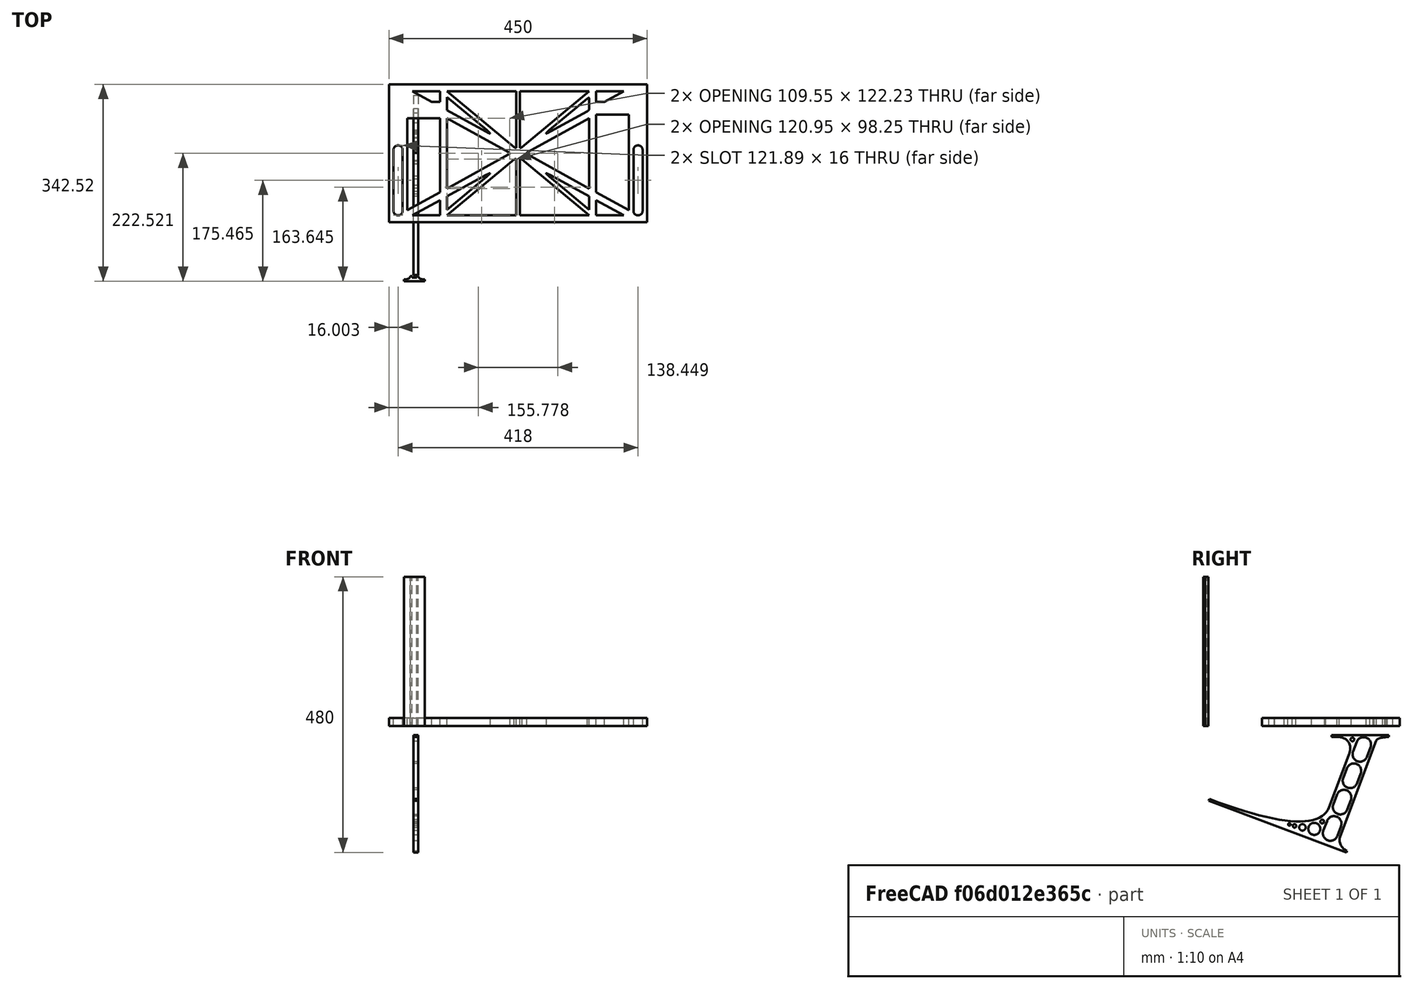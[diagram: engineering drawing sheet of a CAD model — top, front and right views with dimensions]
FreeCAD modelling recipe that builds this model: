
FCSTD DOCUMENT  (FreeCAD 0.19R0.19.2)
Label: laptopStand070
License: All rights reserved
LicenseURL: http://en.wikipedia.org/wiki/All_rights_reserved
objects: Sketcher::SketchObject×3, Part::Extrusion×3
note: 6 computed .brp shape members not serialized (recipe doc carries the construction recipe); baked Part::Feature solids carry a one-line shape summary decoded from their .brp

FEATURE [Sketcher::SketchObject] Sketch
  FullyConstrained = true
  sketch-geometry (140):
    g0: LineSegment StartX=-10.9272 StartY=-82.7794 StartZ=0 EndX=46.0728 EndY=-51.4823 EndZ=0
    g1: LineSegment StartX=366.073 StartY=-91.7794 StartZ=0 EndX=318.073 EndY=-65.424 EndZ=0
    g2: LineSegment StartX=-10.9272 StartY=77.3346 StartZ=0 EndX=-10.9272 EndY=-82.7794 EndZ=0
    g3: LineSegment StartX=375.073 StartY=-82.7794 StartZ=0 EndX=375.073 EndY=83.9235 EndZ=0
    g4: LineSegment StartX=-1.92719 StartY=-91.7794 StartZ=0 EndX=46.0728 EndY=-91.7794 EndZ=0
    g5: LineSegment StartX=318.073 StartY=124.221 StartZ=0 EndX=366.073 EndY=124.221 EndZ=0
    g6: LineSegment StartX=306.073 StartY=124.221 StartZ=0 EndX=189.124 EndY=27.0628 EndZ=0
    g7: LineSegment StartX=58.0728 StartY=-91.7794 StartZ=0 EndX=175.022 EndY=5.37834 EndZ=0
    g8: LineSegment StartX=58.0728 StartY=-81.8102 StartZ=0 EndX=58.0728 EndY=-58.8351 EndZ=0
    g9: LineSegment StartX=306.073 StartY=114.251 StartZ=0 EndX=306.073 EndY=91.2763 EndZ=0
    g10: LineSegment StartX=175.022 StartY=27.0628 StartZ=0 EndX=58.0728 EndY=124.221 EndZ=0
    g11: LineSegment StartX=189.124 StartY=5.37834 StartZ=0 EndX=306.073 EndY=-91.7794 EndZ=0
    g12: LineSegment StartX=306.073 StartY=77.3346 StartZ=0 EndX=306.073 EndY=-44.8935 EndZ=0
    g13: LineSegment StartX=318.073 StartY=83.9235 StartZ=0 EndX=318.073 EndY=-51.4823 EndZ=0
    g14: LineSegment StartX=306.073 StartY=-58.8351 StartZ=0 EndX=306.073 EndY=-81.8102 EndZ=0
    g15: LineSegment StartX=318.073 StartY=-51.4823 StartZ=0 EndX=375.073 EndY=-82.7794 EndZ=0
    g16: LineSegment StartX=318.073 StartY=-65.424 StartZ=0 EndX=318.073 EndY=-91.7794 EndZ=0
    g17: LineSegment StartX=318.073 StartY=-91.7794 StartZ=0 EndX=366.073 EndY=-91.7794 EndZ=0
    g18: LineSegment StartX=58.0728 StartY=-44.8935 StartZ=0 EndX=58.0728 EndY=77.3346 EndZ=0
    g19: LineSegment StartX=46.0728 StartY=-65.424 StartZ=0 EndX=-1.92719 EndY=-91.7794 EndZ=0
    g20: LineSegment StartX=46.0728 StartY=-65.424 StartZ=0 EndX=46.0728 EndY=-91.7794 EndZ=0
    g21: LineSegment StartX=58.0728 StartY=91.2763 StartZ=0 EndX=58.0728 EndY=114.251 EndZ=0
    g22: LineSegment StartX=46.0728 StartY=77.3346 StartZ=0 EndX=46.0728 EndY=-51.4823 EndZ=0
    g23: LineSegment StartX=-42.9272 StartY=136.221 StartZ=0 EndX=-42.9272 EndY=-103.779 EndZ=0
    g24: LineSegment StartX=407.073 StartY=136.221 StartZ=0 EndX=407.073 EndY=-103.779 EndZ=0
    g25: LineSegment StartX=179.022 StartY=27.0628 StartZ=0 EndX=179.022 EndY=124.221 EndZ=0
    g26: LineSegment StartX=185.124 StartY=27.0628 StartZ=0 EndX=185.124 EndY=124.221 EndZ=0
    g27: ArcOfCircle CenterX=-26.9272 CenterY=22.1087 CenterZ=0 NormalX=0 NormalY=0 NormalZ=1 AngleXU=0 Radius=8 StartAngle=1e-16 EndAngle=3.14159
    g28: ArcOfCircle CenterX=-26.9272 CenterY=-83.7794 CenterZ=0 NormalX=0 NormalY=0 NormalZ=1 AngleXU=0 Radius=8 StartAngle=3.14159 EndAngle=6.28319
    g29: LineSegment StartX=-34.9272 StartY=22.1087 StartZ=0 EndX=-34.9272 EndY=-83.7794 EndZ=0
    g30: LineSegment StartX=-18.9272 StartY=22.1087 StartZ=0 EndX=-18.9272 EndY=-83.7794 EndZ=0
    g31: LineSegment StartX=185.124 StartY=-91.7794 StartZ=0 EndX=306.073 EndY=-91.7794 EndZ=0
    g32: LineSegment StartX=179.022 StartY=-91.7794 StartZ=0 EndX=58.0728 EndY=-91.7794 EndZ=0
    g33: LineSegment StartX=306.073 StartY=124.221 StartZ=0 EndX=185.124 EndY=124.221 EndZ=0
    g34: LineSegment StartX=179.022 StartY=124.221 StartZ=0 EndX=58.0728 EndY=124.221 EndZ=0
    g35: ArcOfCircle CenterX=391.073 CenterY=22.1087 CenterZ=0 NormalX=0 NormalY=0 NormalZ=1 AngleXU=0 Radius=8 StartAngle=-4.4e-15 EndAngle=3.14159
    g36: LineSegment StartX=399.073 StartY=22.1087 StartZ=0 EndX=399.073 EndY=-83.7794 EndZ=0
    g37: LineSegment StartX=383.073 StartY=22.1087 StartZ=0 EndX=383.073 EndY=-83.7794 EndZ=0
    g38: ArcOfCircle CenterX=391.073 CenterY=-83.7794 CenterZ=0 NormalX=0 NormalY=0 NormalZ=1 AngleXU=0 Radius=8 StartAngle=3.14159 EndAngle=6.28319
    g39: Circle CenterX=175.022 CenterY=27.0628 CenterZ=0 NormalX=0 NormalY=0 NormalZ=1 AngleXU=0 Radius=1
    g40: Circle CenterX=179.022 CenterY=24.8665 CenterZ=0 NormalX=0 NormalY=0 NormalZ=1 AngleXU=0 Radius=1
    g41: Circle CenterX=179.022 CenterY=27.0628 CenterZ=0 NormalX=0 NormalY=0 NormalZ=1 AngleXU=0 Radius=1
    g42: BSplineCurve PolesCount=3 KnotsCount=2 Degree=2 IsPeriodic=0
    g43: GeomPoint X=175.022 Y=27.0628 Z=0
    g44: GeomPoint X=179.022 Y=27.0628 Z=0
    g45: Circle CenterX=189.124 CenterY=27.0628 CenterZ=0 NormalX=0 NormalY=0 NormalZ=1 AngleXU=0 Radius=1
    g46: Circle CenterX=185.124 CenterY=24.8665 CenterZ=0 NormalX=0 NormalY=0 NormalZ=1 AngleXU=0 Radius=1
    g47: Circle CenterX=185.124 CenterY=27.0628 CenterZ=0 NormalX=0 NormalY=0 NormalZ=1 AngleXU=0 Radius=1
    g48: BSplineCurve PolesCount=3 KnotsCount=2 Degree=2 IsPeriodic=0
    g49: GeomPoint X=189.124 Y=27.0628 Z=0
    g50: GeomPoint X=185.124 Y=27.0628 Z=0
    g51: Circle CenterX=175.022 CenterY=5.37834 CenterZ=0 NormalX=0 NormalY=0 NormalZ=1 AngleXU=0 Radius=1
    g52: Circle CenterX=179.022 CenterY=7.57463 CenterZ=0 NormalX=0 NormalY=0 NormalZ=1 AngleXU=0 Radius=1
    g53: Circle CenterX=179.022 CenterY=5.34704 CenterZ=0 NormalX=0 NormalY=0 NormalZ=1 AngleXU=0 Radius=1
    g54: BSplineCurve PolesCount=3 KnotsCount=2 Degree=2 IsPeriodic=0
    g55: GeomPoint X=175.022 Y=5.37834 Z=0
    g56: GeomPoint X=179.022 Y=5.34704 Z=0
    g57: Circle CenterX=189.124 CenterY=5.37834 CenterZ=0 NormalX=0 NormalY=0 NormalZ=1 AngleXU=0 Radius=1
    g58: Circle CenterX=185.124 CenterY=7.57463 CenterZ=0 NormalX=0 NormalY=0 NormalZ=1 AngleXU=0 Radius=1
    g59: Circle CenterX=185.124 CenterY=5.34704 CenterZ=0 NormalX=0 NormalY=0 NormalZ=1 AngleXU=0 Radius=1
    g60: BSplineCurve PolesCount=3 KnotsCount=2 Degree=2 IsPeriodic=0
    g61: GeomPoint X=189.124 Y=5.37834 Z=0
    g62: GeomPoint X=185.124 Y=5.34704 Z=0
    g63: LineSegment StartX=179.022 StartY=5.34704 StartZ=0 EndX=179.022 EndY=-91.7794 EndZ=0
    g64: LineSegment StartX=185.124 StartY=-91.7794 StartZ=0 EndX=185.124 EndY=5.34704 EndZ=0
    g65: Circle CenterX=165.871 CenterY=18.1458 CenterZ=0 NormalX=0 NormalY=0 NormalZ=1 AngleXU=0 Radius=1
    g66: Circle CenterX=169.377 CenterY=16.2206 CenterZ=0 NormalX=0 NormalY=0 NormalZ=1 AngleXU=0 Radius=1
    g67: Circle CenterX=165.871 CenterY=14.2954 CenterZ=0 NormalX=0 NormalY=0 NormalZ=1 AngleXU=0 Radius=1
    g68: BSplineCurve PolesCount=3 KnotsCount=2 Degree=2 IsPeriodic=0
    g69: GeomPoint X=165.871 Y=18.1458 Z=0
    g70: GeomPoint X=165.871 Y=14.2954 Z=0
    g71: Circle CenterX=198.275 CenterY=18.1458 CenterZ=0 NormalX=0 NormalY=0 NormalZ=1 AngleXU=0 Radius=1
    g72: Circle CenterX=194.768 CenterY=16.2206 CenterZ=0 NormalX=0 NormalY=0 NormalZ=1 AngleXU=0 Radius=1
    g73: Circle CenterX=198.275 CenterY=14.2954 CenterZ=0 NormalX=0 NormalY=0 NormalZ=1 AngleXU=0 Radius=1
    g74: BSplineCurve PolesCount=3 KnotsCount=2 Degree=2 IsPeriodic=0
    g75: GeomPoint X=198.275 Y=18.1458 Z=0
    g76: GeomPoint X=198.275 Y=14.2954 Z=0
    g77: LineSegment StartX=165.871 StartY=18.1458 StartZ=0 EndX=58.0728 EndY=77.3346 EndZ=0
    g78: LineSegment StartX=58.0728 StartY=-44.8935 StartZ=0 EndX=165.871 EndY=14.2954 EndZ=0
    g79: LineSegment StartX=198.275 StartY=18.1458 StartZ=0 EndX=306.073 EndY=77.3346 EndZ=0
    g80: LineSegment StartX=198.275 StartY=14.2954 StartZ=0 EndX=306.073 EndY=-44.8935 EndZ=0
    g81: LineSegment StartX=407.073 StartY=-103.779 StartZ=0 EndX=-42.9272 EndY=-103.779 EndZ=0
    g82: LineSegment StartX=407.073 StartY=136.221 StartZ=0 EndX=-42.9272 EndY=136.221 EndZ=0
    g83: LineSegment StartX=46.0728 StartY=77.3346 StartZ=0 EndX=-10.9272 EndY=77.3346 EndZ=0
    g84: LineSegment StartX=46.0728 StartY=105.865 StartZ=0 EndX=31.5028 EndY=105.865 EndZ=0
    g85: LineSegment StartX=46.0728 StartY=124.221 StartZ=0 EndX=46.0728 EndY=105.865 EndZ=0
    g86: LineSegment StartX=-1.92719 StartY=124.221 StartZ=0 EndX=31.5028 EndY=105.865 EndZ=0
    g87: LineSegment StartX=46.0728 StartY=124.221 StartZ=0 EndX=-1.92719 EndY=124.221 EndZ=0
    g88: LineSegment StartX=318.073 StartY=83.9235 StartZ=0 EndX=375.073 EndY=83.9235 EndZ=0
    g89: LineSegment StartX=318.073 StartY=105.865 StartZ=0 EndX=332.643 EndY=105.865 EndZ=0
    g90: LineSegment StartX=332.643 StartY=105.865 StartZ=0 EndX=366.073 EndY=124.221 EndZ=0
    g91: LineSegment StartX=318.073 StartY=124.221 StartZ=0 EndX=318.073 EndY=105.865 EndZ=0
    g92: Circle CenterX=125.607 CenterY=54.1951 CenterZ=0 NormalX=0 NormalY=0 NormalZ=1 AngleXU=0 Radius=1
    g93: Circle CenterX=139.632 CenterY=46.4944 CenterZ=0 NormalX=0 NormalY=0 NormalZ=1 AngleXU=0 Radius=1
    g94: Circle CenterX=127.325 CenterY=56.7187 CenterZ=0 NormalX=0 NormalY=0 NormalZ=1 AngleXU=0 Radius=1
    g95: BSplineCurve PolesCount=3 KnotsCount=2 Degree=2 IsPeriodic=0
    g96: GeomPoint X=125.607 Y=54.1951 Z=0
    g97: GeomPoint X=127.325 Y=56.7187 Z=0
    g98: LineSegment StartX=127.325 StartY=56.7187 StartZ=0 EndX=58.0728 EndY=114.251 EndZ=0
    g99: LineSegment StartX=58.0728 StartY=91.2763 StartZ=0 EndX=125.607 EndY=54.1951 EndZ=0
    g100: Circle CenterX=236.821 CenterY=56.7187 CenterZ=0 NormalX=0 NormalY=0 NormalZ=1 AngleXU=0 Radius=1
    g101: Circle CenterX=224.513 CenterY=46.4944 CenterZ=0 NormalX=0 NormalY=0 NormalZ=1 AngleXU=0 Radius=1
    g102: Circle CenterX=238.538 CenterY=54.1951 CenterZ=0 NormalX=0 NormalY=0 NormalZ=1 AngleXU=0 Radius=1
    g103: BSplineCurve PolesCount=3 KnotsCount=2 Degree=2 IsPeriodic=0
    g104: GeomPoint X=236.821 Y=56.7187 Z=0
    g105: GeomPoint X=238.538 Y=54.1951 Z=0
    g106: LineSegment StartX=236.821 StartY=56.7187 StartZ=0 EndX=306.073 EndY=114.251 EndZ=0
    g107: LineSegment StartX=238.538 StartY=54.1951 StartZ=0 EndX=306.073 EndY=91.2763 EndZ=0
    g108: Circle CenterX=238.538 CenterY=-21.7539 CenterZ=0 NormalX=0 NormalY=0 NormalZ=1 AngleXU=0 Radius=1
    g109: Circle CenterX=224.513 CenterY=-14.0532 CenterZ=0 NormalX=0 NormalY=0 NormalZ=1 AngleXU=0 Radius=1
    g110: Circle CenterX=236.821 CenterY=-24.2775 CenterZ=0 NormalX=0 NormalY=0 NormalZ=1 AngleXU=0 Radius=1
    g111: BSplineCurve PolesCount=3 KnotsCount=2 Degree=2 IsPeriodic=0
    g112: GeomPoint X=238.538 Y=-21.7539 Z=0
    g113: GeomPoint X=236.821 Y=-24.2775 Z=0
    g114: LineSegment StartX=238.538 StartY=-21.7539 StartZ=0 EndX=306.073 EndY=-58.8351 EndZ=0
    g115: LineSegment StartX=236.821 StartY=-24.2775 StartZ=0 EndX=306.073 EndY=-81.8102 EndZ=0
    g116: Circle CenterX=125.607 CenterY=-21.7539 CenterZ=0 NormalX=0 NormalY=0 NormalZ=1 AngleXU=0 Radius=1
    g117: Circle CenterX=139.632 CenterY=-14.0532 CenterZ=0 NormalX=0 NormalY=0 NormalZ=1 AngleXU=0 Radius=1
    g118: Circle CenterX=127.325 CenterY=-24.2775 CenterZ=0 NormalX=0 NormalY=0 NormalZ=1 AngleXU=0 Radius=1
    g119: BSplineCurve PolesCount=3 KnotsCount=2 Degree=2 IsPeriodic=0
    g120: GeomPoint X=125.607 Y=-21.7539 Z=0
    g121: GeomPoint X=127.325 Y=-24.2775 Z=0
    g122: LineSegment StartX=125.607 StartY=-21.7539 StartZ=0 EndX=58.0728 EndY=-58.8351 EndZ=0
    g123: LineSegment StartX=127.325 StartY=-24.2775 StartZ=0 EndX=58.0728 EndY=-81.8102 EndZ=0
    g124: LineSegment StartX=306.073 StartY=114.251 StartZ=0 EndX=306.073 EndY=110.251 EndZ=0
    g125: LineSegment StartX=306.073 StartY=114.251 StartZ=0 EndX=302.996 EndY=111.695 EndZ=0
    g126: LineSegment StartX=306.073 StartY=91.2763 StartZ=0 EndX=306.073 EndY=95.2763 EndZ=0
    g127: LineSegment StartX=306.073 StartY=91.2763 StartZ=0 EndX=302.567 EndY=89.3511 EndZ=0
    g128: Circle CenterX=302.996 CenterY=111.695 CenterZ=0 NormalX=0 NormalY=0 NormalZ=1 AngleXU=0 Radius=1
    g129: Circle CenterX=306.073 CenterY=114.251 CenterZ=0 NormalX=0 NormalY=0 NormalZ=1 AngleXU=0 Radius=1
    g130: Circle CenterX=306.073 CenterY=110.251 CenterZ=0 NormalX=0 NormalY=0 NormalZ=1 AngleXU=0 Radius=1
    g131: BSplineCurve PolesCount=3 KnotsCount=2 Degree=2 IsPeriodic=0
    g132: GeomPoint X=302.996 Y=111.695 Z=0
    g133: GeomPoint X=306.073 Y=110.251 Z=0
    g134: Circle CenterX=306.073 CenterY=95.2763 CenterZ=0 NormalX=0 NormalY=0 NormalZ=1 AngleXU=0 Radius=1
    g135: Circle CenterX=306.073 CenterY=91.2763 CenterZ=0 NormalX=0 NormalY=0 NormalZ=1 AngleXU=0 Radius=1
    g136: Circle CenterX=302.567 CenterY=89.3511 CenterZ=0 NormalX=0 NormalY=0 NormalZ=1 AngleXU=0 Radius=1
    g137: BSplineCurve PolesCount=3 KnotsCount=2 Degree=2 IsPeriodic=0
    g138: GeomPoint X=306.073 Y=95.2763 Z=0
    g139: GeomPoint X=302.567 Y=89.3511 Z=0
  constraints (257):
    c: Horizontal(g4)
    c: Horizontal(g5)
    c: Tangent(g12,g14)
    c: Coincident(g13,g15)
    c: Coincident(g16,g1)
    c: Tangent(g13,g16)
    c: Tangent(g8,g18)
    c: Coincident(g20,g19)
    c: Coincident(g0,g22)
    c: Tangent(g18,g21)
    c: Block(g10)
    c: Block(g6)
    c: Block(g15)
    c: Block(g3)
    c: Block(g14)
    c: Block(g1)
    c: Block(g16)
    c: Block(g11)
    c: Block(g7)
    c: Block(g20)
    c: Block(g19)
    c: Block(g0)
    c: Block(g2)
    c: Block(g21)
    c: Block(g12)
    c: Block(g5)
    c: Block(g17)
    c: Block(g4)
    c: Vertical(g23)
    c: Vertical(g24)
    c: Block(g24)
    c: Block(g23)
    c: Vertical(g25)
    c: Vertical(g26)
    c: Block(g25)
    c: Block(g26)
    c: Tangent(g27,g30) = 1.5708
    c: Tangent(g27,g29) = -1.5708
    c: Tangent(g29,g28) = -1.5708
    c: Tangent(g30,g28) = 1.5708
    c: Vertical(g29)
    c: Equal(g27,g28)
    c: Block(g30)
    c: Block(g29)
    c: Coincident(g31,g11)
    c: Horizontal(g31)
    c: Coincident(g32,g7)
    c: Horizontal(g32)
    c: Coincident(g33,g6)
    c: Coincident(g33,g26)
    c: Horizontal(g33)
    c: Coincident(g34,g25)
    c: Coincident(g34,g10)
    c: Horizontal(g34)
    c: Tangent(g35,g36) = 1.5708
    c: Tangent(g36,g38) = 1.5708
    c: Equal(g35,g38)
    c: Coincident(g37,g35)
    c: Coincident(g37,g38)
    c: Block(g36)
    c: Block(g37)
    c: Coincident(g42,g10)
    c: Weight(g39) = 1
    c: Equal(g39,g40)
    c: Equal(g39,g41)
    c: Coincident(g42,g25)
    c: InternalAlignment(g39,g42)
    c: InternalAlignment(g40,g42)
    c: InternalAlignment(g41,g42)
    c: InternalAlignment(g43,g42)
    c: InternalAlignment(g44,g42)
    c: Coincident(g48,g6)
    c: Weight(g45) = 1
    c: Equal(g45,g46)
    c: Equal(g45,g47)
    c: Coincident(g48,g26)
    c: InternalAlignment(g45,g48)
    c: InternalAlignment(g46,g48)
    c: InternalAlignment(g47,g48)
    c: InternalAlignment(g49,g48)
    c: InternalAlignment(g50,g48)
    c: Block(g48)
    c: Block(g42)
    c: Coincident(g54,g7)
    c: Weight(g51) = 1
    c: Equal(g51,g52)
    c: Equal(g51,g53)
    c: InternalAlignment(g51,g54)
    c: InternalAlignment(g52,g54)
    c: InternalAlignment(g53,g54)
    c: InternalAlignment(g55,g54)
    c: InternalAlignment(g56,g54)
    c: Weight(g57) = 1
    c: Equal(g57,g58)
    c: Equal(g57,g59)
    c: InternalAlignment(g57,g60)
    c: InternalAlignment(g58,g60)
    c: InternalAlignment(g59,g60)
    c: InternalAlignment(g61,g60)
    c: InternalAlignment(g62,g60)
    c: Block(g60)
    c: Block(g54)
    c: Coincident(g63,g54)
    c: Coincident(g63,g32)
    c: Vertical(g63)
    c: Coincident(g64,g31)
    c: Coincident(g64,g60)
    c: Vertical(g64)
    c: Weight(g65) = 1
    c: Equal(g65,g66)
    c: Equal(g65,g67)
    c: InternalAlignment(g65,g68)
    c: InternalAlignment(g66,g68)
    c: InternalAlignment(g67,g68)
    c: InternalAlignment(g69,g68)
    c: InternalAlignment(g70,g68)
    c: Weight(g71) = 1
    c: Equal(g71,g72)
    c: Equal(g71,g73)
    c: InternalAlignment(g71,g74)
    c: InternalAlignment(g72,g74)
    c: InternalAlignment(g73,g74)
    c: InternalAlignment(g75,g74)
    c: InternalAlignment(g76,g74)
    c: Block(g68)
    c: Block(g74)
    c: Coincident(g77,g68)
    c: Coincident(g77,g18)
    c: Coincident(g78,g18)
    c: Coincident(g78,g68)
    c: Coincident(g79,g74)
    c: Coincident(g79,g12)
    c: Coincident(g80,g74)
    c: Coincident(g80,g12)
    c: Block(g18)
    c: Coincident(g81,g24)
    c: Coincident(g81,g23)
    c: Horizontal(g81)
    c: Distance(g81) = 450
    c: Coincident(g82,g24)
    c: Coincident(g82,g23)
    c: Horizontal(g82)
    c: Horizontal(g83)
    c: Coincident(g22,g83)
    c: Horizontal(g84)
    c: Vertical(g85)
    c: Block(g85)
    c: Block(g84)
    c: Block(g83)
    c: Distance(g85) = 18.3554
    c: Coincident(g87,g85)
    c: Coincident(g87,g86)
    c: Horizontal(g87)
    c: Block(g87)
    c: Block(g86)
    c: Coincident(g84,g86)
    c: Coincident(g2,g83)
    c: Coincident(g88,g13)
    c: Horizontal(g88)
    c: Horizontal(g89)
    c: Block(g88)
    c: Block(g9)
    c: Coincident(g90,g5)
    c: Coincident(g91,g5)
    c: Coincident(g91,g89)
    c: Vertical(g91)
    c: Block(g91)
    c: Coincident(g89,g90)
    c: Block(g90)
    c: Coincident(g3,g88)
    c: Weight(g92) = 1
    c: Equal(g92,g93)
    c: Equal(g92,g94)
    c: InternalAlignment(g92,g95)
    c: InternalAlignment(g93,g95)
    c: InternalAlignment(g94,g95)
    c: InternalAlignment(g96,g95)
    c: InternalAlignment(g97,g95)
    c: Block(g95)
    c: Coincident(g98,g95)
    c: Coincident(g98,g21)
    c: Coincident(g99,g21)
    c: Coincident(g99,g95)
    c: Weight(g100) = 1
    c: Equal(g100,g101)
    c: Equal(g100,g102)
    c: InternalAlignment(g100,g103)
    c: InternalAlignment(g101,g103)
    c: InternalAlignment(g102,g103)
    c: InternalAlignment(g104,g103)
    c: InternalAlignment(g105,g103)
    c: Block(g103)
    c: Coincident(g106,g103)
    c: Coincident(g106,g9)
    c: Coincident(g107,g103)
    c: Coincident(g107,g9)
    c: Weight(g108) = 1
    c: Equal(g108,g109)
    c: Equal(g108,g110)
    c: InternalAlignment(g108,g111)
    c: InternalAlignment(g109,g111)
    c: InternalAlignment(g110,g111)
    c: InternalAlignment(g112,g111)
    c: InternalAlignment(g113,g111)
    c: Block(g111)
    c: Coincident(g114,g111)
    c: Coincident(g114,g14)
    c: Coincident(g115,g111)
    c: Coincident(g115,g14)
    c: Weight(g116) = 1
    c: Equal(g116,g117)
    c: Equal(g116,g118)
    c: InternalAlignment(g116,g119)
    c: InternalAlignment(g117,g119)
    c: InternalAlignment(g118,g119)
    c: InternalAlignment(g120,g119)
    c: InternalAlignment(g121,g119)
    c: Block(g119)
    c: Coincident(g122,g119)
    c: Coincident(g122,g8)
    c: Coincident(g123,g119)
    c: Coincident(g123,g8)
    c: Block(g8)
    c: Vertical(g124)
    c: Vertical(g126)
    c: Distance(g126) = 4
    c: Distance(g124) = 4
    c: Distance(g125) = 4
    c: Distance(g127) = 4
    c: Parallel(g127,g107)
    c: Parallel(g125,g106)
    c: Coincident(g124,g9)
    c: Coincident(g125,g9)
    c: Coincident(g9,g126)
    c: Coincident(g127,g9)
    c: Coincident(g131,g125)
    c: Weight(g128) = 1
    c: Equal(g128,g129)
    c: Coincident(g129,g9)
    c: Equal(g128,g130)
    c: Coincident(g131,g124)
    c: InternalAlignment(g128,g131)
    c: InternalAlignment(g129,g131)
    c: InternalAlignment(g130,g131)
    c: InternalAlignment(g132,g131)
    c: InternalAlignment(g133,g131)
    c: Coincident(g137,g126)
    c: Weight(g134) = 1
    c: Equal(g134,g135)
    c: Coincident(g135,g9)
    c: Equal(g134,g136)
    c: Coincident(g137,g127)
    c: InternalAlignment(g134,g137)
    c: InternalAlignment(g135,g137)
    c: InternalAlignment(g136,g137)
    c: InternalAlignment(g138,g137)
    c: InternalAlignment(g139,g137)
FEATURE [Sketcher::SketchObject] Sketch001
  FullyConstrained = true
  MapMode = 4
  Placement = pos=(0,0,0) rot=(0.57735,0.57735,0.57735;2.0944rad)
  Support = -> [Sketch]
  sketch-geometry (46):
    g0: BSplineCurve PolesCount=3 KnotsCount=2 Degree=2 IsPeriodic=0
    g1: ArcOfCircle CenterX=73.1223 CenterY=-32.291 CenterZ=0 NormalX=0 NormalY=0 NormalZ=1 AngleXU=0 Radius=13 StartAngle=5.92268 EndAngle=9.06428
    g2: ArcOfCircle CenterX=66.7816 CenterY=-49.1439 CenterZ=0 NormalX=0 NormalY=0 NormalZ=1 AngleXU=0 Radius=13 StartAngle=2.78068 EndAngle=5.92131
    g3: ArcOfCircle CenterX=55.9263 CenterY=-78.1807 CenterZ=0 NormalX=0 NormalY=0 NormalZ=1 AngleXU=0 Radius=13 StartAngle=5.92268 EndAngle=9.06428
    g4: ArcOfCircle CenterX=49.5884 CenterY=-95.0342 CenterZ=0 NormalX=0 NormalY=0 NormalZ=1 AngleXU=0 Radius=13 StartAngle=2.78068 EndAngle=5.92131
    g5: ArcOfCircle CenterX=38.7206 CenterY=-124.067 CenterZ=0 NormalX=0 NormalY=0 NormalZ=1 AngleXU=0 Radius=13 StartAngle=5.92268 EndAngle=9.06428
    g6: ArcOfCircle CenterX=32.3875 CenterY=-140.92 CenterZ=0 NormalX=0 NormalY=0 NormalZ=1 AngleXU=0 Radius=13 StartAngle=2.78068 EndAngle=5.92131
    g7: ArcOfCircle CenterX=21.4715 CenterY=-169.934 CenterZ=0 NormalX=0 NormalY=0 NormalZ=1 AngleXU=0 Radius=13 StartAngle=5.92268 EndAngle=9.06428
    g8: ArcOfCircle CenterX=15.1336 CenterY=-186.787 CenterZ=0 NormalX=0 NormalY=0 NormalZ=1 AngleXU=0 Radius=13 StartAngle=2.78068 EndAngle=5.92131
    g9-g12: Circle x4 (B-spline internal-alignment scaffolding for g13; pole/knot coordinates omitted)
    g13: BSplineCurve PolesCount=4 KnotsCount=2 Degree=3 IsPeriodic=0
    g14: GeomPoint X=28.8094 Y=-19.0875 Z=0
    g15: GeomPoint X=47.0443 Y=-50.4712 Z=0
    g16: Circle CenterX=53.5586 CenterY=-23.2695 CenterZ=0 NormalX=0 NormalY=0 NormalZ=1 AngleXU=0 Radius=3.24518
    g17: Circle CenterX=-195.441 CenterY=-127.082 CenterZ=0 NormalX=0 NormalY=0 NormalZ=1 AngleXU=0 Radius=1
    g18: Circle CenterX=-8.24091 CenterY=-197.481 CenterZ=0 NormalX=0 NormalY=0 NormalZ=1 AngleXU=0 Radius=1
    g19: Circle CenterX=12.8789 CenterY=-141.321 CenterZ=0 NormalX=0 NormalY=0 NormalZ=1 AngleXU=0 Radius=1
    g20: BSplineCurve PolesCount=3 KnotsCount=2 Degree=2 IsPeriodic=0
    g21: GeomPoint X=-195.441 Y=-127.082 Z=0
    g22: GeomPoint X=12.8789 Y=-141.321 Z=0
    g23: Circle CenterX=-12.8016 CenterY=-179.036 CenterZ=0 NormalX=0 NormalY=0 NormalZ=1 AngleXU=0 Radius=10.5072
    g24: Circle CenterX=0.933922 CenterY=-166.43 CenterZ=0 NormalX=0 NormalY=0 NormalZ=1 AngleXU=0 Radius=3.26661
    g25: Circle CenterX=-33.5518 CenterY=-176.44 CenterZ=0 NormalX=0 NormalY=0 NormalZ=1 AngleXU=0 Radius=5.64388
    g26: Circle CenterX=-47.2366 CenterY=-173.859 CenterZ=0 NormalX=0 NormalY=0 NormalZ=1 AngleXU=0 Radius=3.01653
    g27: Circle CenterX=-56.2595 CenterY=-171.456 CenterZ=0 NormalX=0 NormalY=0 NormalZ=1 AngleXU=0 Radius=2.12826
    g28: ArcOfCircle CenterX=51.2151 CenterY=-198.473 CenterZ=0 NormalX=0 NormalY=0 NormalZ=1 AngleXU=0 Radius=20 StartAngle=2.78189 EndAngle=4.35269
    g29: LineSegment StartX=32.4951 StartY=-191.433 StartZ=0 EndX=94.6578 EndY=-26.1352 EndZ=0
    g30: LineSegment StartX=43.1192 StartY=-220.001 StartZ=0 EndX=-196.497 EndY=-129.89 EndZ=0
    g31: LineSegment StartX=43.1192 StartY=-220.001 StartZ=0 EndX=44.1752 EndY=-217.193 EndZ=0
    g32: LineSegment StartX=117.223 StartY=-19.0875 StartZ=0 EndX=117.223 EndY=-16.0875 EndZ=0
    g33: LineSegment StartX=117.223 StartY=-16.0875 StartZ=0 EndX=17.2232 EndY=-16.0875 EndZ=0
    g34: LineSegment StartX=17.2232 StartY=-16.0875 StartZ=0 EndX=17.2232 EndY=-19.0875 EndZ=0
    g35: LineSegment StartX=28.8094 StartY=-19.0875 StartZ=0 EndX=17.2232 EndY=-19.0875 EndZ=0
    g36: LineSegment StartX=47.0443 StartY=-50.4712 StartZ=0 EndX=12.8789 EndY=-141.321 EndZ=0
    g37: LineSegment StartX=-195.441 StartY=-127.082 StartZ=0 EndX=-196.497 EndY=-129.89 EndZ=0
    g38: LineSegment StartX=85.2866 StartY=-36.8766 StartZ=0 EndX=78.9396 EndY=-53.7463 EndZ=0
    g39: LineSegment StartX=60.9579 StartY=-27.7053 StartZ=0 EndX=54.6191 EndY=-44.5532 EndZ=0
    g40: LineSegment StartX=68.0907 StartY=-82.7664 StartZ=0 EndX=61.7465 EndY=-99.6365 EndZ=0
    g41: LineSegment StartX=43.7619 StartY=-73.595 StartZ=0 EndX=37.426 EndY=-90.4435 EndZ=0
    g42: LineSegment StartX=50.885 StartY=-128.652 StartZ=0 EndX=44.5456 EndY=-145.522 EndZ=0
    g43: LineSegment StartX=26.5562 StartY=-119.481 StartZ=0 EndX=20.2251 EndY=-136.329 EndZ=0
    g44: LineSegment StartX=9.3071 StartY=-165.349 StartZ=0 EndX=2.97115 EndY=-182.197 EndZ=0
    g45: LineSegment StartX=33.6358 StartY=-174.52 StartZ=0 EndX=27.2917 EndY=-191.39 EndZ=0
  constraints (71):
    c: Block(g0)
    c: Block(g1)
    c: Block(g2)
    c: Block(g4)
    c: Block(g3)
    c: Block(g6)
    c: Block(g5)
    c: Block(g8)
    c: Block(g7)
    c: Weight(g9) = 1
    c: Equal(g9,g10)
    c: Equal(g9,g11)
    c: Equal(g9,g12)
    c: InternalAlignment(g9-g12 -> g13) x4
    c: InternalAlignment(g14,g13)
    c: InternalAlignment(g15,g13)
    c: Block(g16)
    c: Weight(g17) = 1
    c: Equal(g17,g18)
    c: Equal(g17,g19)
    c: InternalAlignment(g17,g20)
    c: InternalAlignment(g18,g20)
    c: InternalAlignment(g19,g20)
    c: InternalAlignment(g21,g20)
    c: InternalAlignment(g22,g20)
    c: Block(g20)
    c: Block(g23)
    c: Block(g24)
    c: Block(g25)
    c: Block(g26)
    c: Block(g27)
    c: Block(g28)
    c: Coincident(g29,g28)
    c: Coincident(g29,g0)
    c: Block(g13)
    c: Coincident(g31,g30)
    c: Coincident(g31,g28)
    c: Block(g31)
    c: Coincident(g32,g0)
    c: Vertical(g32)
    c: Coincident(g33,g32)
    c: Horizontal(g33)
    c: Coincident(g34,g33)
    c: Vertical(g34)
    c: Block(g33)
    c: Coincident(g35,g13)
    c: Coincident(g35,g34)
    c: Horizontal(g35)
    c: Coincident(g36,g13)
    c: Coincident(g36,g20)
    c: Coincident(g37,g20)
    c: Coincident(g37,g30)
    c: Block(g30)
    c: Coincident(g38,g1)
    c: Coincident(g38,g2)
    c: Coincident(g39,g1)
    c: Coincident(g39,g2)
    c: Coincident(g40,g3)
    c: Coincident(g40,g4)
    c: Coincident(g41,g3)
    c: Coincident(g41,g4)
    c: Coincident(g42,g5)
    c: Coincident(g42,g6)
    c: Coincident(g43,g5)
    c: Coincident(g43,g6)
    c: Coincident(g44,g7)
    c: Coincident(g44,g8)
    c: Coincident(g45,g7)
    c: Coincident(g45,g8)
    c: Distance(g30) = 256
    c: Distance(g33) = 100
FEATURE [Part::Extrusion] Extrude002
  Base = -> Sketch001
  Dir = (1,0,0)
  DirMode = 2
  FaceMakerClass = Part::FaceMakerBullseye
  LengthFwd = 8
  LengthRev = 0
  Solid = true
  Symmetric = false
FEATURE [Sketcher::SketchObject] Sketch002
  FullyConstrained = true
  sketch-geometry (20):
    g0: LineSegment StartX=-2.77179 StartY=-200.304 StartZ=0 EndX=5.22821 EndY=-200.304 EndZ=0
    g1: LineSegment StartX=5.22821 StartY=-200.304 StartZ=0 EndX=5.22821 EndY=-197.304 EndZ=0
    g2: LineSegment StartX=-2.77179 StartY=-200.304 StartZ=0 EndX=-2.77179 EndY=-197.304 EndZ=0
    g3: LineSegment StartX=5.22821 StartY=-197.304 StartZ=0 EndX=8.22821 EndY=-197.304 EndZ=0
    g4: LineSegment StartX=-2.77179 StartY=-197.304 StartZ=0 EndX=-5.77179 EndY=-197.304 EndZ=0
    g5: LineSegment StartX=19.2282 StartY=-203.304 StartZ=0 EndX=19.2282 EndY=-206.304 EndZ=0
    g6: LineSegment StartX=-16.7718 StartY=-203.304 StartZ=0 EndX=-16.7718 EndY=-206.304 EndZ=0
    g7: LineSegment StartX=-16.7718 StartY=-206.304 StartZ=0 EndX=19.2282 EndY=-206.304 EndZ=0
    g8: Circle CenterX=-16.7718 CenterY=-203.304 CenterZ=0 NormalX=0 NormalY=0 NormalZ=1 AngleXU=0 Radius=1
    g9: Circle CenterX=-5.77179 CenterY=-203.304 CenterZ=0 NormalX=0 NormalY=0 NormalZ=1 AngleXU=0 Radius=1
    g10: Circle CenterX=-5.77179 CenterY=-197.304 CenterZ=0 NormalX=0 NormalY=0 NormalZ=1 AngleXU=0 Radius=1
    g11: BSplineCurve PolesCount=3 KnotsCount=2 Degree=2 IsPeriodic=0
    g12: GeomPoint X=-16.7718 Y=-203.304 Z=0
    g13: GeomPoint X=-5.77179 Y=-197.304 Z=0
    g14: Circle CenterX=19.2282 CenterY=-203.304 CenterZ=0 NormalX=0 NormalY=0 NormalZ=1 AngleXU=0 Radius=1
    g15: Circle CenterX=8.22821 CenterY=-203.304 CenterZ=0 NormalX=0 NormalY=0 NormalZ=1 AngleXU=0 Radius=1
    g16: Circle CenterX=8.22821 CenterY=-197.304 CenterZ=0 NormalX=0 NormalY=0 NormalZ=1 AngleXU=0 Radius=1
    g17: BSplineCurve PolesCount=3 KnotsCount=2 Degree=2 IsPeriodic=0
    g18: GeomPoint X=19.2282 Y=-203.304 Z=0
    g19: GeomPoint X=8.22821 Y=-197.304 Z=0
  constraints (41):
    c: Horizontal(g0)
    c: Distance(g0) = 8
    c: Coincident(g1,g0)
    c: Vertical(g1)
    c: Distance(g1) = 3
    c: Coincident(g2,g0)
    c: Vertical(g2)
    c: Distance(g2) = 3
    c: Coincident(g3,g1)
    c: Horizontal(g3)
    c: Distance(g3) = 3
    c: Coincident(g4,g2)
    c: Horizontal(g4)
    c: Distance(g4) = 3
    c: Vertical(g5)
    c: Vertical(g6)
    c: Coincident(g7,g6)
    c: Coincident(g7,g5)
    c: Weight(g8) = 1
    c: Equal(g8,g9)
    c: Equal(g8,g10)
    c: Coincident(g11,g4)
    c: InternalAlignment(g8,g11)
    c: InternalAlignment(g9,g11)
    c: InternalAlignment(g10,g11)
    c: InternalAlignment(g12,g11)
    c: InternalAlignment(g13,g11)
    c: Coincident(g17,g5)
    c: Weight(g14) = 1
    c: Equal(g14,g15)
    c: Equal(g14,g16)
    c: Coincident(g17,g3)
    c: InternalAlignment(g14,g17)
    c: InternalAlignment(g15,g17)
    c: InternalAlignment(g16,g17)
    c: InternalAlignment(g18,g17)
    c: InternalAlignment(g19,g17)
    c: Block(g7)
    c: Block(g17)
    c: Block(g11)
    c: Block(g6)
FEATURE [Part::Extrusion] Extrude003
  Base = -> Sketch002
  Dir = (0,0,1)
  DirMode = 2
  FaceMakerClass = Part::FaceMakerBullseye
  LengthFwd = 260
  LengthRev = 0
  Solid = true
  Symmetric = false
FEATURE [Part::Extrusion] Extrude
  Base = -> Sketch
  Dir = (0,0,1)
  DirMode = 2
  FaceMakerClass = Part::FaceMakerBullseye
  LengthFwd = 14
  LengthRev = 0
  Solid = true
  Symmetric = false
